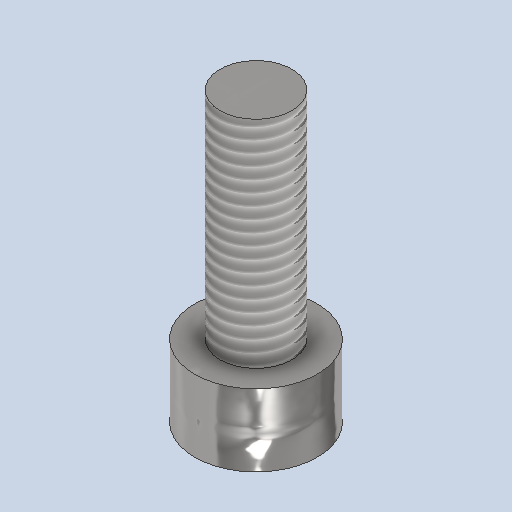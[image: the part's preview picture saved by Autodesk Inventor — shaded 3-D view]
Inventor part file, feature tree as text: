
AUTODESK INVENTOR PART (.ipt)
format: ipt  version: 2024.2 (Build 282272000, 272)  size: 178,176 bytes
history: native  units: mm
features: sketch x2, revolve x1, thread x1, extrude x1
ambient origin geometry x8: Origin, YZ Plane, XZ Plane, XY Plane, X Axis, Y Axis, Z Axis, Center Point
bodies: Solid1 (feature_tree)
feature tree (5):
  revolve  "Revolution1"  [1 undecoded]
  thread  "Thread1"  [1 undecoded]
  extrude  "Extrusion1"  [1 undecoded]
  sketch  "Sketch1"  dims[d4=90.0deg d5=10.0mm d6=0.0mm d0=0.0mm]
  sketch  "Sketch2"
note: 3 required parameter values undecoded (feature->parameter linkage not recoverable at this tier; creation-order binding heuristic only, values carry confidence <= 0.55)